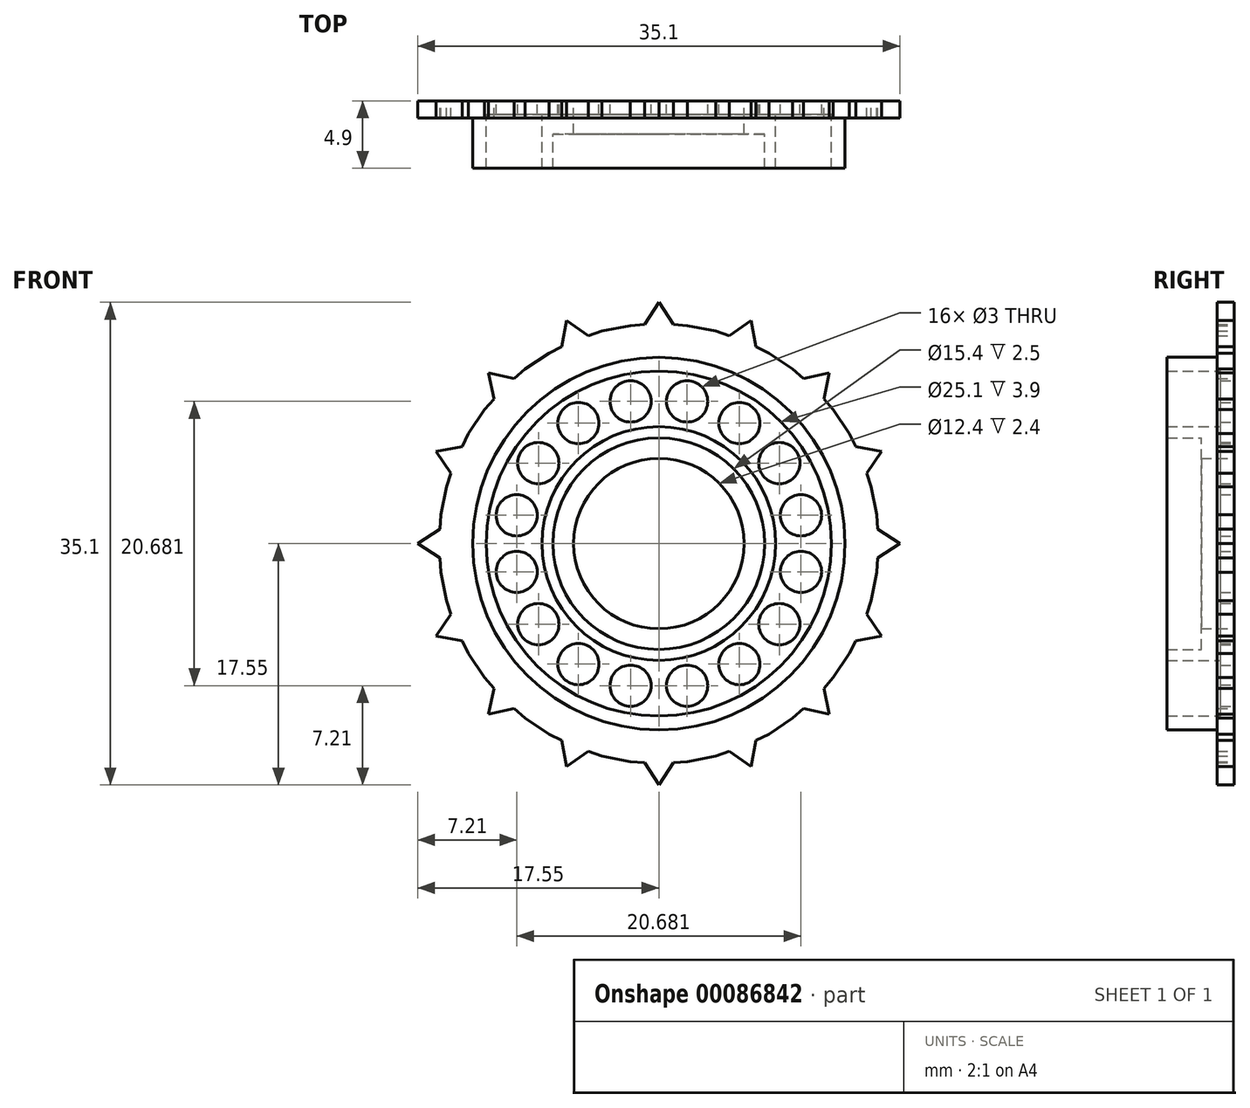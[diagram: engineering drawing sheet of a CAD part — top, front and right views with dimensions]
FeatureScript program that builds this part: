
annotation { "Feature Type Name" : "Feature", "Feature Type Description" : "" }
export const myFeature = defineFeature(function(context is Context, id is Id, definition is map)
    precondition{}
    {
        {
            var Q0;
            Q0=qCreatedBy(makeId("Front.planeOp"),FACE);
            var sketch = newSketch(context, id + "F0", { "sketchPlane" : qUnion([Q0])});
            skCircle(sketch, "E0", {"center": v(0, 0) * mm, "radius": 13.55 * mm});
            skCircle(sketch, "E1", {"center": v(0, 0) * mm, "radius": 12.55 * mm});
            skCircle(sketch, "E2", {"center": v(0, 0) * mm, "radius": 7.7 * mm});
            skCircle(sketch, "E3", {"center": v(0, 0) * mm, "radius": 8.5 * mm});
            skLineSegment(sketch, "E4.1", {"start": v(2.09, 15.86) * mm, "end": v(4.14, 15.45) * mm});
            skLineSegment(sketch, "E4.4", {"start": v(8, 13.86) * mm, "end": v(9.74, 12.7) * mm});
            skLineSegment(sketch, "E4.7", {"start": v(12.7, 9.74) * mm, "end": v(13.86, 8) * mm});
            skLineSegment(sketch, "E4.10", {"start": v(15.45, 4.14) * mm, "end": v(15.86, 2.09) * mm});
            skLineSegment(sketch, "E4.13", {"start": v(15.86, -2.09) * mm, "end": v(15.45, -4.14) * mm});
            skLineSegment(sketch, "E4.16", {"start": v(13.86, -8) * mm, "end": v(12.7, -9.74) * mm});
            skLineSegment(sketch, "E4.19", {"start": v(9.74, -12.7) * mm, "end": v(8, -13.86) * mm});
            skLineSegment(sketch, "E4.22", {"start": v(4.14, -15.45) * mm, "end": v(2.09, -15.86) * mm});
            skLineSegment(sketch, "E4.25", {"start": v(-2.09, -15.86) * mm, "end": v(-4.14, -15.45) * mm});
            skLineSegment(sketch, "E4.28", {"start": v(-8, -13.86) * mm, "end": v(-9.74, -12.7) * mm});
            skLineSegment(sketch, "E4.31", {"start": v(-12.7, -9.74) * mm, "end": v(-13.86, -8) * mm});
            skLineSegment(sketch, "E4.34", {"start": v(-15.45, -4.14) * mm, "end": v(-15.86, -2.09) * mm});
            skLineSegment(sketch, "E4.37", {"start": v(-15.86, 2.09) * mm, "end": v(-15.45, 4.14) * mm});
            skLineSegment(sketch, "E4.40", {"start": v(-13.86, 8) * mm, "end": v(-12.7, 9.74) * mm});
            skLineSegment(sketch, "E4.43", {"start": v(-9.74, 12.7) * mm, "end": v(-8, 13.86) * mm});
            skLineSegment(sketch, "E4.46", {"start": v(-4.14, 15.45) * mm, "end": v(-2.09, 15.86) * mm});
            skLineSegment(sketch, "E5", {"start": v(-1.04, 15.93) * mm, "end": v(0, 17.55) * mm});
            skLineSegment(sketch, "E6", {"start": v(0, 17.55) * mm, "end": v(1.04, 15.93) * mm});
            skLineSegment(sketch, "E7", {"start": v(-6.72, 16.21) * mm, "end": v(-7.06, 14.32) * mm});
            skLineSegment(sketch, "E8", {"start": v(-6.72, 16.21) * mm, "end": v(-5.13, 15.12) * mm});
            skLineSegment(sketch, "E9", {"start": v(6.72, 16.21) * mm, "end": v(5.13, 15.12) * mm});
            skLineSegment(sketch, "E10", {"start": v(6.72, 16.21) * mm, "end": v(7.06, 14.32) * mm});
            skLineSegment(sketch, "E11", {"start": v(10.53, 12) * mm, "end": v(12.4, 12.4) * mm});
            skLineSegment(sketch, "E12", {"start": v(12.4, 12.4) * mm, "end": v(12, 10.53) * mm});
            skLineSegment(sketch, "E13", {"start": v(14.32, 7.06) * mm, "end": v(16.21, 6.72) * mm});
            skLineSegment(sketch, "E14", {"start": v(16.21, 6.72) * mm, "end": v(15.12, 5.13) * mm});
            skLineSegment(sketch, "E15", {"start": v(15.93, 1.04) * mm, "end": v(17.55, 0) * mm});
            skLineSegment(sketch, "E16", {"start": v(17.55, 0) * mm, "end": v(15.93, -1.04) * mm});
            skLineSegment(sketch, "E17", {"start": v(-10.53, 12) * mm, "end": v(-12.4, 12.4) * mm});
            skLineSegment(sketch, "E18", {"start": v(-12, 10.53) * mm, "end": v(-12.4, 12.4) * mm});
            skLineSegment(sketch, "E19", {"start": v(-14.32, 7.06) * mm, "end": v(-16.21, 6.72) * mm});
            skLineSegment(sketch, "E20", {"start": v(-15.12, 5.13) * mm, "end": v(-16.21, 6.72) * mm});
            skLineSegment(sketch, "E21", {"start": v(-15.93, 1.04) * mm, "end": v(-17.55, 0) * mm});
            skLineSegment(sketch, "E22", {"start": v(-15.93, -1.04) * mm, "end": v(-17.55, 0) * mm});
            skLineSegment(sketch, "E23", {"start": v(-15.12, -5.13) * mm, "end": v(-16.21, -6.72) * mm});
            skLineSegment(sketch, "E24", {"start": v(-14.32, -7.06) * mm, "end": v(-16.21, -6.72) * mm});
            skLineSegment(sketch, "E25", {"start": v(-12, -10.53) * mm, "end": v(-12.4, -12.4) * mm});
            skLineSegment(sketch, "E26", {"start": v(-10.53, -12) * mm, "end": v(-12.4, -12.4) * mm});
            skLineSegment(sketch, "E27", {"start": v(-7.06, -14.32) * mm, "end": v(-6.72, -16.21) * mm});
            skLineSegment(sketch, "E28", {"start": v(-5.13, -15.12) * mm, "end": v(-6.72, -16.21) * mm});
            skLineSegment(sketch, "E29", {"start": v(-1.04, -15.93) * mm, "end": v(0, -17.55) * mm});
            skLineSegment(sketch, "E30", {"start": v(1.04, -15.93) * mm, "end": v(0, -17.55) * mm});
            skLineSegment(sketch, "E31", {"start": v(5.13, -15.12) * mm, "end": v(6.72, -16.21) * mm});
            skLineSegment(sketch, "E32", {"start": v(7.06, -14.32) * mm, "end": v(6.72, -16.21) * mm});
            skLineSegment(sketch, "E33", {"start": v(10.53, -12) * mm, "end": v(12.4, -12.4) * mm});
            skLineSegment(sketch, "E34", {"start": v(12, -10.53) * mm, "end": v(12.4, -12.4) * mm});
            skLineSegment(sketch, "E35", {"start": v(14.32, -7.06) * mm, "end": v(16.21, -6.72) * mm});
            skLineSegment(sketch, "E36", {"start": v(15.12, -5.13) * mm, "end": v(16.21, -6.72) * mm});
            skLineSegment(sketch, "E37", {"start": v(0, 12.55) * mm, "end": v(0, 8.5) * mm, "construction": true});
            skCircle(sketch, "E38.cCircle", {"center": v(0, 0) * mm, "radius": 10.34 * mm, "construction": true});
            skLineSegment(sketch, "E38.0", {"start": v(-2.06, 10.34) * mm, "end": v(2.06, 10.34) * mm, "construction": true});
            skLineSegment(sketch, "E38.1", {"start": v(2.06, 10.34) * mm, "end": v(5.86, 8.77) * mm, "construction": true});
            skLineSegment(sketch, "E38.2", {"start": v(5.86, 8.77) * mm, "end": v(8.77, 5.86) * mm, "construction": true});
            skLineSegment(sketch, "E38.3", {"start": v(8.77, 5.86) * mm, "end": v(10.34, 2.06) * mm, "construction": true});
            skLineSegment(sketch, "E38.4", {"start": v(10.34, 2.06) * mm, "end": v(10.34, -2.06) * mm, "construction": true});
            skLineSegment(sketch, "E38.5", {"start": v(10.34, -2.06) * mm, "end": v(8.77, -5.86) * mm, "construction": true});
            skLineSegment(sketch, "E38.6", {"start": v(8.77, -5.86) * mm, "end": v(5.86, -8.77) * mm, "construction": true});
            skLineSegment(sketch, "E38.7", {"start": v(5.86, -8.77) * mm, "end": v(2.06, -10.34) * mm, "construction": true});
            skLineSegment(sketch, "E38.8", {"start": v(2.06, -10.34) * mm, "end": v(-2.06, -10.34) * mm, "construction": true});
            skLineSegment(sketch, "E38.9", {"start": v(-2.06, -10.34) * mm, "end": v(-5.86, -8.77) * mm, "construction": true});
            skLineSegment(sketch, "E38.10", {"start": v(-5.86, -8.77) * mm, "end": v(-8.77, -5.86) * mm, "construction": true});
            skLineSegment(sketch, "E38.11", {"start": v(-8.77, -5.86) * mm, "end": v(-10.34, -2.06) * mm, "construction": true});
            skLineSegment(sketch, "E38.12", {"start": v(-10.34, -2.06) * mm, "end": v(-10.34, 2.06) * mm, "construction": true});
            skLineSegment(sketch, "E38.13", {"start": v(-10.34, 2.06) * mm, "end": v(-8.77, 5.86) * mm, "construction": true});
            skLineSegment(sketch, "E38.14", {"start": v(-8.77, 5.86) * mm, "end": v(-5.86, 8.77) * mm, "construction": true});
            skLineSegment(sketch, "E38.15", {"start": v(-5.86, 8.77) * mm, "end": v(-2.06, 10.34) * mm, "construction": true});
            skCircle(sketch, "E39", {"center": v(-5.86, 8.77) * mm, "radius": 1.5 * mm});
            skCircle(sketch, "E40", {"center": v(-2.06, 10.34) * mm, "radius": 1.5 * mm});
            skCircle(sketch, "E41", {"center": v(2.06, 10.34) * mm, "radius": 1.5 * mm});
            skCircle(sketch, "E42", {"center": v(5.86, 8.77) * mm, "radius": 1.5 * mm});
            skCircle(sketch, "E43", {"center": v(8.77, 5.86) * mm, "radius": 1.5 * mm});
            skCircle(sketch, "E44", {"center": v(10.34, 2.06) * mm, "radius": 1.5 * mm});
            skCircle(sketch, "E45", {"center": v(10.34, -2.06) * mm, "radius": 1.5 * mm});
            skCircle(sketch, "E46", {"center": v(8.77, -5.86) * mm, "radius": 1.5 * mm});
            skCircle(sketch, "E47", {"center": v(5.86, -8.77) * mm, "radius": 1.5 * mm});
            skCircle(sketch, "E48", {"center": v(2.06, -10.34) * mm, "radius": 1.5 * mm});
            skCircle(sketch, "E49", {"center": v(-2.06, -10.34) * mm, "radius": 1.5 * mm});
            skCircle(sketch, "E50", {"center": v(-5.86, -8.77) * mm, "radius": 1.5 * mm});
            skCircle(sketch, "E51", {"center": v(-8.77, -5.86) * mm, "radius": 1.5 * mm});
            skCircle(sketch, "E52", {"center": v(-10.34, -2.06) * mm, "radius": 1.5 * mm});
            skCircle(sketch, "E53", {"center": v(-10.34, 2.06) * mm, "radius": 1.5 * mm});
            skCircle(sketch, "E54", {"center": v(-8.77, 5.86) * mm, "radius": 1.5 * mm});
            skLineSegment(sketch, "E55", {"start": v(-15.45, 4.14) * mm, "end": v(-15.12, 5.13) * mm});
            skLineSegment(sketch, "E56", {"start": v(-14.32, 7.06) * mm, "end": v(-13.86, 8) * mm});
            skLineSegment(sketch, "E57", {"start": v(-12.7, 9.74) * mm, "end": v(-12, 10.53) * mm});
            skLineSegment(sketch, "E58", {"start": v(-10.53, 12) * mm, "end": v(-9.74, 12.7) * mm});
            skLineSegment(sketch, "E59", {"start": v(-8, 13.86) * mm, "end": v(-7.06, 14.32) * mm});
            skLineSegment(sketch, "E60", {"start": v(-5.13, 15.12) * mm, "end": v(-4.14, 15.45) * mm});
            skLineSegment(sketch, "E61", {"start": v(-2.09, 15.86) * mm, "end": v(-1.04, 15.93) * mm});
            skLineSegment(sketch, "E62", {"start": v(1.04, 15.93) * mm, "end": v(2.09, 15.86) * mm});
            skLineSegment(sketch, "E63", {"start": v(4.14, 15.45) * mm, "end": v(5.13, 15.12) * mm});
            skLineSegment(sketch, "E64", {"start": v(7.06, 14.32) * mm, "end": v(8, 13.86) * mm});
            skLineSegment(sketch, "E65", {"start": v(9.74, 12.7) * mm, "end": v(10.53, 12) * mm});
            skLineSegment(sketch, "E66", {"start": v(12, 10.53) * mm, "end": v(12.7, 9.74) * mm});
            skLineSegment(sketch, "E67", {"start": v(13.86, 8) * mm, "end": v(14.32, 7.06) * mm});
            skLineSegment(sketch, "E68", {"start": v(15.12, 5.13) * mm, "end": v(15.45, 4.14) * mm});
            skLineSegment(sketch, "E69", {"start": v(15.86, 2.09) * mm, "end": v(15.93, 1.04) * mm});
            skLineSegment(sketch, "E70", {"start": v(15.93, -1.04) * mm, "end": v(15.86, -2.09) * mm});
            skLineSegment(sketch, "E71", {"start": v(15.45, -4.14) * mm, "end": v(15.12, -5.13) * mm});
            skLineSegment(sketch, "E72", {"start": v(14.32, -7.06) * mm, "end": v(13.86, -8) * mm});
            skLineSegment(sketch, "E73", {"start": v(12.7, -9.74) * mm, "end": v(12, -10.53) * mm});
            skLineSegment(sketch, "E74", {"start": v(10.53, -12) * mm, "end": v(9.74, -12.7) * mm});
            skLineSegment(sketch, "E75", {"start": v(8, -13.86) * mm, "end": v(7.06, -14.32) * mm});
            skLineSegment(sketch, "E76", {"start": v(5.13, -15.12) * mm, "end": v(4.14, -15.45) * mm});
            skLineSegment(sketch, "E77", {"start": v(2.09, -15.86) * mm, "end": v(1.04, -15.93) * mm});
            skLineSegment(sketch, "E78", {"start": v(-1.04, -15.93) * mm, "end": v(-2.09, -15.86) * mm});
            skLineSegment(sketch, "E79", {"start": v(-4.14, -15.45) * mm, "end": v(-5.13, -15.12) * mm});
            skLineSegment(sketch, "E80", {"start": v(-7.06, -14.32) * mm, "end": v(-8, -13.86) * mm});
            skLineSegment(sketch, "E81", {"start": v(-9.74, -12.7) * mm, "end": v(-10.53, -12) * mm});
            skLineSegment(sketch, "E82", {"start": v(-12, -10.53) * mm, "end": v(-12.7, -9.74) * mm});
            skLineSegment(sketch, "E83", {"start": v(-13.86, -8) * mm, "end": v(-14.32, -7.06) * mm});
            skLineSegment(sketch, "E84", {"start": v(-15.12, -5.13) * mm, "end": v(-15.45, -4.14) * mm});
            skLineSegment(sketch, "E85", {"start": v(-15.86, -2.09) * mm, "end": v(-15.93, -1.04) * mm});
            skLineSegment(sketch, "E86", {"start": v(-15.93, 1.04) * mm, "end": v(-15.86, 2.09) * mm});
            skSolve(sketch);
        }
        {
            var Q0;
            Q0=makeQuery(id+"F0.imprint","IMPRINT",FACE,{"disambiguationData":[TD([[makeQuery(id+"F0.imprint","IMPRINT",EDGE,{"derivedFrom":sQuery(id+"F0.wireOp",EDGE,"E0")}),-1.0]])]});
            extrude(context, id + "F1", {"entities" : qUnion([Q0]), "depth" : 2.5 * mm / 2});
        }
        {
            var Q0;
            Q0=makeQuery(id+"F0.imprint","IMPRINT",FACE,{"disambiguationData":[TD([[makeQuery(id+"F0.imprint","IMPRINT",EDGE,{"derivedFrom":sQuery(id+"F0.wireOp",EDGE,"E0")}),1.0]])]});
            extrude(context, id + "F2", {"entities" : qUnion([Q0]), "operationType" : NewBodyOperationType.ADD, "depth" : 9.8 * mm / 2});
        }
        {
            var Q0;
            Q0=makeQuery(id+"F0.imprint","IMPRINT",FACE,{"disambiguationData":[TD([[makeQuery(id+"F0.imprint","IMPRINT",EDGE,{"derivedFrom":sQuery(id+"F0.wireOp",EDGE,"E1")}),1.0]])]});
            extrude(context, id + "F3", {"entities" : qUnion([Q0]), "operationType" : NewBodyOperationType.ADD, "depth" : 2 * mm / 2});
        }
        {
            var Q0;
            Q0=makeQuery(id+"F0.imprint","IMPRINT",FACE,{"disambiguationData":[TD([[makeQuery(id+"F0.imprint","IMPRINT",EDGE,{"derivedFrom":sQuery(id+"F0.wireOp",EDGE,"E2")}),-1.0]])]});
            extrude(context, id + "F4", {"entities" : qUnion([Q0]), "operationType" : NewBodyOperationType.ADD, "depth" : 9.8 * mm / 2});
        }
        {
            var Q0;
            Q0=makeQuery(id+"F4.opExtrude","CAP_FACE",FACE,{"disambiguationData":[OSD([sQuery(id+"F0.wireOp",EDGE,"E2"),sQuery(id+"F0.wireOp",EDGE,"E3")])],"isStart":true});
            var sketch = newSketch(context, id + "F5", { "sketchPlane" : qUnion([Q0])});
            skCircle(sketch, "E87", {"center": v(0, 0) * mm, "radius": 6.2 * mm});
            skSolve(sketch);
        }
        {
            var Q0;
            Q0=makeQuery(id+"F5.imprint","IMPRINT",FACE,{"disambiguationData":[TD([[makeQuery(id+"F5.imprint","IMPRINT",EDGE,{"derivedFrom":sQuery(id+"F5.wireOp",EDGE,"E87")}),-1.0]])]});
            extrude(context, id + "F6", {"entities" : qUnion([Q0]), "operationType" : NewBodyOperationType.ADD, "oppositeDirection" : true, "depth" : 2.4 * mm});
        }
    });
